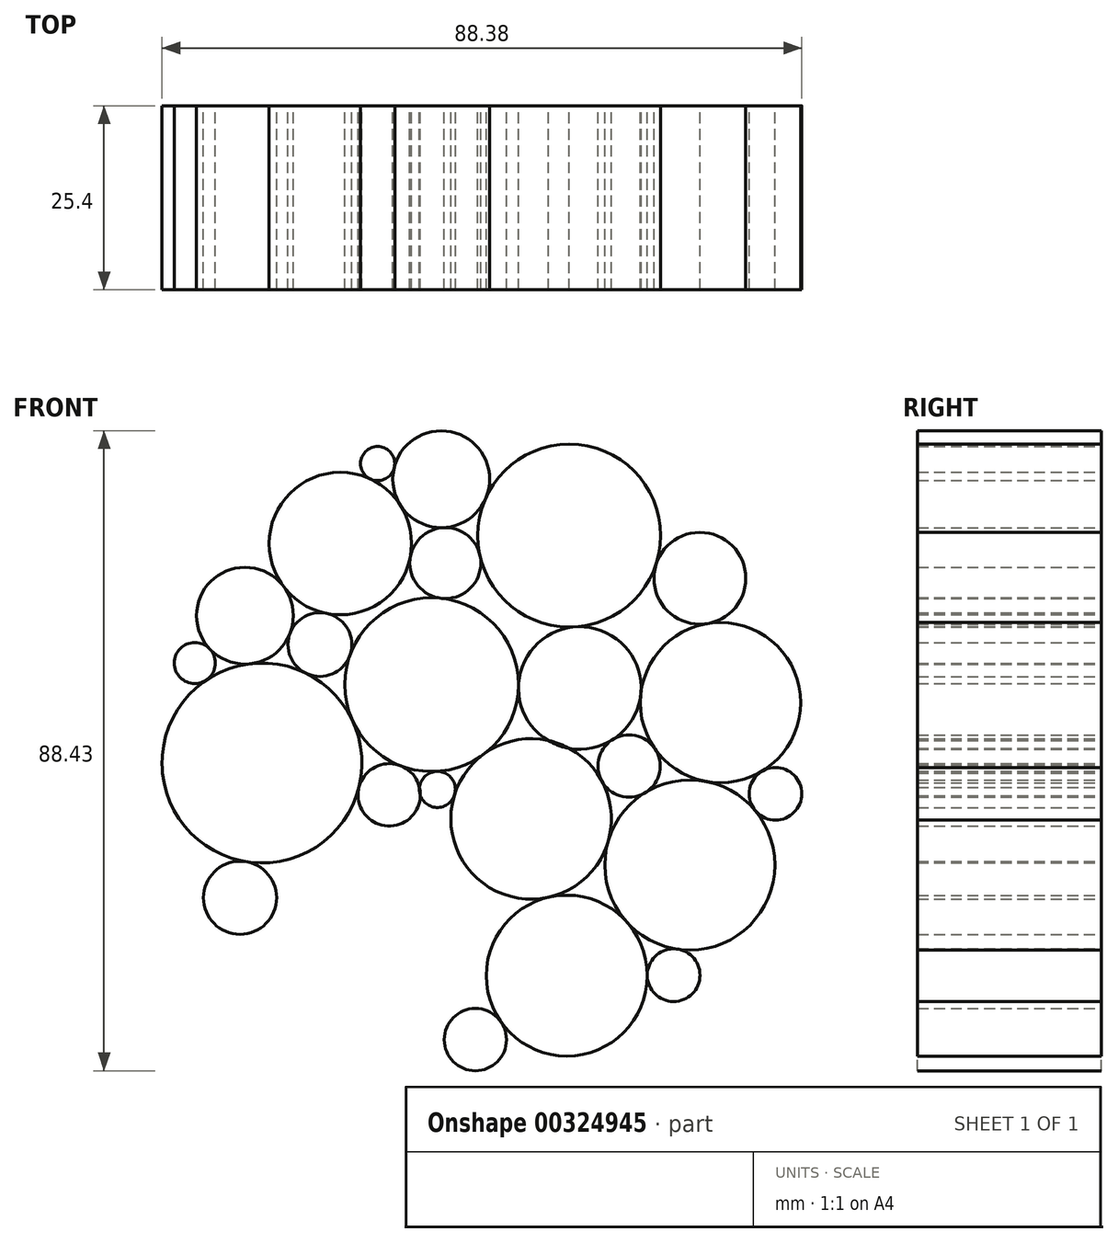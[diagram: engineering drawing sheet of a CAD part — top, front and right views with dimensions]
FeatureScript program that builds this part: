
annotation { "Feature Type Name" : "Feature", "Feature Type Description" : "" }
export const myFeature = defineFeature(function(context is Context, id is Id, definition is map)
    precondition{}
    {
        {
            var Q0;
            Q0=qCreatedBy(makeId("Front.planeOp"),FACE);
            var sketch = newSketch(context, id + "F0", { "sketchPlane" : qUnion([Q0])});
            skCircle(sketch, "E0", {"center": v(0, 0) * mm, "radius": 44.45 * mm});
            skCircle(sketch, "E1", {"center": v(-19.76, 28.42) * mm, "radius": 9.84 * mm});
            skPoint(sketch, "E1.first.point", {"position": v(-25.38, 36.5) * mm});
            skPoint(sketch, "E1.second.point", {"position": v(-25.38, 36.5) * mm});
            skPoint(sketch, "E1.third.point", {"position": v(-13.44, 20.87) * mm});
            skCircle(sketch, "E2", {"center": v(-32.95, 18.45) * mm, "radius": 6.69 * mm});
            skPoint(sketch, "E2.first.point", {"position": v(-27.61, 22.48) * mm});
            skPoint(sketch, "E2.second.point", {"position": v(-38.78, 21.72) * mm});
            skPoint(sketch, "E2.third.point", {"position": v(-30.05, 12.42) * mm});
            skCircle(sketch, "E3", {"center": v(-22.6, 14.46) * mm, "radius": 4.4 * mm});
            skPoint(sketch, "E3.first.point", {"position": v(-26.7, 16.05) * mm});
            skPoint(sketch, "E3.second.point", {"position": v(-21.72, 18.77) * mm});
            skPoint(sketch, "E3.third.point", {"position": v(-18.7, 12.42) * mm});
            skCircle(sketch, "E4", {"center": v(-5.83, 37.3) * mm, "radius": 6.7 * mm});
            skPoint(sketch, "E4.first.point", {"position": v(-6.86, 43.92) * mm});
            skPoint(sketch, "E4.second.point", {"position": v(-11.47, 33.7) * mm});
            skPoint(sketch, "E4.third.point", {"position": v(0, 34.02) * mm});
            skCircle(sketch, "E5", {"center": v(-5.26, 25.72) * mm, "radius": 4.9 * mm});
            skPoint(sketch, "E5.first.point", {"position": v(-5.5, 30.62) * mm});
            skPoint(sketch, "E5.second.point", {"position": v(-10.09, 26.62) * mm});
            skPoint(sketch, "E5.third.point", {"position": v(-0.38, 26.15) * mm});
            skCircle(sketch, "E6", {"center": v(-14.12, -25.7) * mm, "radius": 15.13 * mm});
            skPoint(sketch, "E6.first.point", {"position": v(-21.4, -38.96) * mm});
            skPoint(sketch, "E6.second.point", {"position": v(-21.4, -38.96) * mm});
            skPoint(sketch, "E6.third.point", {"position": v(-7.62, -12.04) * mm});
            skCircle(sketch, "E7", {"center": v(-30.59, -1.9) * mm, "radius": 13.8 * mm});
            skPoint(sketch, "E7.first.point", {"position": v(-44.33, -3.3) * mm});
            skPoint(sketch, "E7.second.point", {"position": v(-22.73, -13.26) * mm});
            skPoint(sketch, "E7.third.point", {"position": v(-32.18, 11.8) * mm});
            skCircle(sketch, "E8", {"center": v(-7.16, 8.92) * mm, "radius": 12 * mm});
            skPoint(sketch, "E8.first.point", {"position": v(-18.05, 3.89) * mm});
            skPoint(sketch, "E8.second.point", {"position": v(-18.45, 12.97) * mm});
            skPoint(sketch, "E8.third.point", {"position": v(-5.81, 20.85) * mm});
            skCircle(sketch, "E9", {"center": v(-13.01, -6.3) * mm, "radius": 4.3 * mm});
            skPoint(sketch, "E9.first.point", {"position": v(-11.47, -2.28) * mm});
            skPoint(sketch, "E9.second.point", {"position": v(-13.26, -10.6) * mm});
            skPoint(sketch, "E9.third.point", {"position": v(-17.2, -5.26) * mm});
            skCircle(sketch, "E10", {"center": v(-33.63, -20.53) * mm, "radius": 5.05 * mm});
            skPoint(sketch, "E10.first.point", {"position": v(-32.81, -15.54) * mm});
            skPoint(sketch, "E10.second.point", {"position": v(-28.74, -21.82) * mm});
            skPoint(sketch, "E10.third.point", {"position": v(-37.94, -23.16) * mm});
            skCircle(sketch, "E11", {"center": v(11.86, 29.52) * mm, "radius": 12.64 * mm});
            skPoint(sketch, "E11.first.point", {"position": v(16.57, 41.24) * mm});
            skPoint(sketch, "E11.second.point", {"position": v(0.3, 34.61) * mm});
            skPoint(sketch, "E11.third.point", {"position": v(17.65, 18.29) * mm});
            skCircle(sketch, "E12", {"center": v(6.59, -9.63) * mm, "radius": 11.09 * mm});
            skPoint(sketch, "E12.first.point", {"position": v(-0.01, -0.72) * mm});
            skPoint(sketch, "E12.second.point", {"position": v(-2.17, -16.43) * mm});
            skPoint(sketch, "E12.third.point", {"position": v(17.59, -8.25) * mm});
            skCircle(sketch, "E13", {"center": v(11.52, -31.28) * mm, "radius": 11.12 * mm});
            skPoint(sketch, "E13.first.point", {"position": v(0.66, -28.92) * mm});
            skPoint(sketch, "E13.second.point", {"position": v(9.05, -20.44) * mm});
            skPoint(sketch, "E13.third.point", {"position": v(15.36, -41.71) * mm});
            skCircle(sketch, "E14", {"center": v(13.31, 8.47) * mm, "radius": 8.47 * mm});
            skPoint(sketch, "E14.first.point", {"position": v(12.73, 16.91) * mm});
            skPoint(sketch, "E14.second.point", {"position": v(4.84, 8.65) * mm});
            skPoint(sketch, "E14.third.point", {"position": v(11.86, 0.12) * mm});
            skCircle(sketch, "E15", {"center": v(28.52, -16) * mm, "radius": 11.75 * mm});
            skPoint(sketch, "E15.first.point", {"position": v(17.24, -12.72) * mm});
            skPoint(sketch, "E15.second.point", {"position": v(19.78, -23.85) * mm});
            skPoint(sketch, "E15.third.point", {"position": v(38.77, -21.74) * mm});
            skCircle(sketch, "E16", {"center": v(32.75, 6.43) * mm, "radius": 11.07 * mm});
            skPoint(sketch, "E16.first.point", {"position": v(43.62, 8.57) * mm});
            skPoint(sketch, "E16.second.point", {"position": v(30.7, -4.45) * mm});
            skPoint(sketch, "E16.third.point", {"position": v(21.73, 7.58) * mm});
            skCircle(sketch, "E17", {"center": v(29.9, 23.62) * mm, "radius": 6.34 * mm});
            skPoint(sketch, "E17.first.point", {"position": v(23.87, 25.6) * mm});
            skPoint(sketch, "E17.second.point", {"position": v(30.94, 17.36) * mm});
            skPoint(sketch, "E17.third.point", {"position": v(34.88, 27.55) * mm});
            skCircle(sketch, "E18", {"center": v(-39.87, 11.91) * mm, "radius": 2.84 * mm});
            skPoint(sketch, "E18.first.point", {"position": v(-42.59, 12.72) * mm});
            skPoint(sketch, "E18.second.point", {"position": v(-37.8, 13.86) * mm});
            skPoint(sketch, "E18.third.point", {"position": v(-38.29, 9.56) * mm});
            skCircle(sketch, "E19", {"center": v(40.35, -6.16) * mm, "radius": 3.63 * mm});
            skPoint(sketch, "E19.first.point", {"position": v(38.47, -3.05) * mm});
            skPoint(sketch, "E19.second.point", {"position": v(37.56, -8.48) * mm});
            skPoint(sketch, "E19.third.point", {"position": v(43.94, -6.7) * mm});
            skCircle(sketch, "E20", {"center": v(-1.1, -40.13) * mm, "radius": 4.3 * mm});
            skPoint(sketch, "E20.first.point", {"position": v(2.42, -37.66) * mm});
            skPoint(sketch, "E20.second.point", {"position": v(-4, -36.93) * mm});
            skPoint(sketch, "E20.third.point", {"position": v(-1.23, -44.43) * mm});
            skCircle(sketch, "E21", {"center": v(20.12, -2.33) * mm, "radius": 4.3 * mm});
            skPoint(sketch, "E21.first.point", {"position": v(16.35, -4.37) * mm});
            skPoint(sketch, "E21.second.point", {"position": v(17.83, 1.3) * mm});
            skPoint(sketch, "E21.third.point", {"position": v(23.65, 0.12) * mm});
            skCircle(sketch, "E22", {"center": v(26.28, -31.22) * mm, "radius": 3.64 * mm});
            skPoint(sketch, "E22.first.point", {"position": v(26.8, -27.62) * mm});
            skPoint(sketch, "E22.second.point", {"position": v(22.63, -31.24) * mm});
            skPoint(sketch, "E22.third.point", {"position": v(28.62, -34) * mm});
            skCircle(sketch, "E23", {"center": v(-6.36, -5.55) * mm, "radius": 2.5 * mm});
            skPoint(sketch, "E23.first.point", {"position": v(-8.84, -5.26) * mm});
            skPoint(sketch, "E23.second.point", {"position": v(-6.5, -3.06) * mm});
            skPoint(sketch, "E23.third.point", {"position": v(-3.99, -6.3) * mm});
            skCircle(sketch, "E24", {"center": v(-14.61, 39.47) * mm, "radius": 2.36 * mm});
            skPoint(sketch, "E24.first.point", {"position": v(-15.43, 41.69) * mm});
            skPoint(sketch, "E24.second.point", {"position": v(-15.6, 37.34) * mm});
            skPoint(sketch, "E24.third.point", {"position": v(-12.32, 38.9) * mm});
            skPoint(sketch, "E25.third.point", {"position": v(-11.66, -40.62) * mm});
            skSolve(sketch);
        }
        {
            var Q0;
            {var subQ0=sQuery(id+"F0.wireOp",EDGE,"E1");var subQ4=makeQuery(id+"F0.imprint","INTERSECT",VERTEX,{"derivedFrom":[subQ0,sQuery(id+"F0.wireOp",EDGE,"E24")]});Q0=makeQuery(id+"F0.imprint","IMPRINT",FACE,{"disambiguationData":[TD([[makeQuery(id+"F0.imprint","IMPRINT",EDGE,{"disambiguationData":[TD([[subQ4,1.0]])],"derivedFrom":subQ0}),1.0]])]});}
            var Q1;
            {var subQ0=sQuery(id+"F0.wireOp",EDGE,"E24");var subQ1=makeQuery(id+"F0.imprint","INTERSECT",VERTEX,{"derivedFrom":[sQuery(id+"F0.wireOp",EDGE,"E0"),subQ0]});Q1=makeQuery(id+"F0.imprint","IMPRINT",FACE,{"disambiguationData":[TD([[makeQuery(id+"F0.imprint","IMPRINT",EDGE,{"disambiguationData":[TD([[subQ1,-1.0]])],"derivedFrom":subQ0}),1.0]])]});}
            var Q2;
            {var subQ0=sQuery(id+"F0.wireOp",EDGE,"E4");var subQ5=makeQuery(id+"F0.imprint","INTERSECT",VERTEX,{"derivedFrom":[sQuery(id+"F0.wireOp",EDGE,"E0"),subQ0]});Q2=makeQuery(id+"F0.imprint","IMPRINT",FACE,{"disambiguationData":[TD([[makeQuery(id+"F0.imprint","IMPRINT",EDGE,{"disambiguationData":[TD([[subQ5,-1.0]])],"derivedFrom":subQ0}),1.0]])]});}
            var Q3;
            {var subQ0=sQuery(id+"F0.wireOp",EDGE,"E5");var subQ1=makeQuery(id+"F0.imprint","INTERSECT",VERTEX,{"derivedFrom":[sQuery(id+"F0.wireOp",EDGE,"E4"),subQ0]});Q3=makeQuery(id+"F0.imprint","IMPRINT",FACE,{"disambiguationData":[TD([[makeQuery(id+"F0.imprint","IMPRINT",EDGE,{"disambiguationData":[TD([[subQ1,1.0]])],"derivedFrom":subQ0}),1.0]])]});}
            var Q4;
            {var subQ0=sQuery(id+"F0.wireOp",EDGE,"E11");var subQ5=makeQuery(id+"F0.imprint","INTERSECT",VERTEX,{"derivedFrom":[sQuery(id+"F0.wireOp",EDGE,"E0"),subQ0]});Q4=makeQuery(id+"F0.imprint","IMPRINT",FACE,{"disambiguationData":[TD([[makeQuery(id+"F0.imprint","IMPRINT",EDGE,{"disambiguationData":[TD([[subQ5,-1.0]])],"derivedFrom":subQ0}),1.0]])]});}
            var Q5;
            {var subQ0=sQuery(id+"F0.wireOp",EDGE,"E8");var subQ4=makeQuery(id+"F0.imprint","INTERSECT",VERTEX,{"derivedFrom":[sQuery(id+"F0.wireOp",EDGE,"E3"),subQ0]});Q5=makeQuery(id+"F0.imprint","IMPRINT",FACE,{"disambiguationData":[TD([[makeQuery(id+"F0.imprint","IMPRINT",EDGE,{"disambiguationData":[TD([[subQ4,1.0]])],"derivedFrom":subQ0}),1.0]])]});}
            var Q6;
            {var subQ0=sQuery(id+"F0.wireOp",EDGE,"E6");var subQ4=makeQuery(id+"F0.imprint","INTERSECT",VERTEX,{"derivedFrom":[sQuery(id+"F0.wireOp",EDGE,"E9"),subQ0]});Q6=makeQuery(id+"F0.imprint","IMPRINT",FACE,{"disambiguationData":[TD([[makeQuery(id+"F0.imprint","IMPRINT",EDGE,{"disambiguationData":[TD([[subQ4,1.0]])],"derivedFrom":subQ0}),1.0]])]});}
            var Q7;
            {var subQ0=sQuery(id+"F0.wireOp",EDGE,"E12");var subQ4=sQuery(id+"F0.wireOp",EDGE,"E14");var subQ6=makeQuery(id+"F0.imprint","INTERSECT",VERTEX,{"disambiguationData":[OD(0.0)],"derivedFrom":[subQ0,subQ4]});Q7=makeQuery(id+"F0.imprint","IMPRINT",FACE,{"disambiguationData":[TD([[makeQuery(id+"F0.imprint","IMPRINT",EDGE,{"disambiguationData":[TD([[subQ6,1.0]])],"derivedFrom":subQ0}),1.0]])]});}
            var Q8;
            {var subQ0=sQuery(id+"F0.wireOp",EDGE,"E14");var subQ1=sQuery(id+"F0.wireOp",EDGE,"E12");var subQ2=makeQuery(id+"F0.imprint","INTERSECT",VERTEX,{"disambiguationData":[OD(0.0)],"derivedFrom":[subQ1,subQ0]});Q8=makeQuery(id+"F0.imprint","IMPRINT",FACE,{"disambiguationData":[TD([[makeQuery(id+"F0.imprint","IMPRINT",EDGE,{"disambiguationData":[TD([[subQ2,-1.0]])],"derivedFrom":subQ1}),-1.0]])]});}
            var Q9;
            {var subQ0=sQuery(id+"F0.wireOp",EDGE,"E9");var subQ5=makeQuery(id+"F0.imprint","INTERSECT",VERTEX,{"derivedFrom":[sQuery(id+"F0.wireOp",EDGE,"E8"),subQ0]});Q9=makeQuery(id+"F0.imprint","IMPRINT",FACE,{"disambiguationData":[TD([[makeQuery(id+"F0.imprint","IMPRINT",EDGE,{"disambiguationData":[TD([[subQ5,1.0]])],"derivedFrom":subQ0}),1.0]])]});}
            var Q10;
            {var subQ0=sQuery(id+"F0.wireOp",EDGE,"E23");var subQ1=sQuery(id+"F0.wireOp",EDGE,"E9");var subQ2=makeQuery(id+"F0.imprint","INTERSECT",VERTEX,{"disambiguationData":[OD(0.0)],"derivedFrom":[subQ1,subQ0]});Q10=makeQuery(id+"F0.imprint","IMPRINT",FACE,{"disambiguationData":[TD([[makeQuery(id+"F0.imprint","IMPRINT",EDGE,{"disambiguationData":[TD([[subQ2,1.0]])],"derivedFrom":subQ1}),-1.0]])]});}
            var Q11;
            {var subQ0=sQuery(id+"F0.wireOp",EDGE,"E7");var subQ4=sQuery(id+"F0.wireOp",EDGE,"E0");var subQ5=makeQuery(id+"F0.imprint","INTERSECT",VERTEX,{"disambiguationData":[OD(0.0)],"derivedFrom":[subQ4,subQ0]});Q11=makeQuery(id+"F0.imprint","IMPRINT",FACE,{"disambiguationData":[TD([[makeQuery(id+"F0.imprint","IMPRINT",EDGE,{"disambiguationData":[TD([[subQ5,-1.0]])],"derivedFrom":subQ4}),1.0]])]});}
            var Q12;
            {var subQ0=sQuery(id+"F0.wireOp",EDGE,"E10");var subQ1=makeQuery(id+"F0.imprint","INTERSECT",VERTEX,{"derivedFrom":[sQuery(id+"F0.wireOp",EDGE,"E0"),subQ0]});Q12=makeQuery(id+"F0.imprint","IMPRINT",FACE,{"disambiguationData":[TD([[makeQuery(id+"F0.imprint","IMPRINT",EDGE,{"disambiguationData":[TD([[subQ1,1.0]])],"derivedFrom":subQ0}),1.0]])]});}
            var Q13;
            {var subQ0=sQuery(id+"F0.wireOp",EDGE,"E3");var subQ1=makeQuery(id+"F0.imprint","INTERSECT",VERTEX,{"derivedFrom":[sQuery(id+"F0.wireOp",EDGE,"E1"),subQ0]});Q13=makeQuery(id+"F0.imprint","IMPRINT",FACE,{"disambiguationData":[TD([[makeQuery(id+"F0.imprint","IMPRINT",EDGE,{"disambiguationData":[TD([[subQ1,-1.0]])],"derivedFrom":subQ0}),1.0]])]});}
            var Q14;
            {var subQ0=sQuery(id+"F0.wireOp",EDGE,"E2");var subQ4=makeQuery(id+"F0.imprint","INTERSECT",VERTEX,{"derivedFrom":[sQuery(id+"F0.wireOp",EDGE,"E0"),subQ0]});Q14=makeQuery(id+"F0.imprint","IMPRINT",FACE,{"disambiguationData":[TD([[makeQuery(id+"F0.imprint","IMPRINT",EDGE,{"disambiguationData":[TD([[subQ4,1.0]])],"derivedFrom":subQ0}),1.0]])]});}
            var Q15;
            {var subQ0=sQuery(id+"F0.wireOp",EDGE,"E18");var subQ1=makeQuery(id+"F0.imprint","INTERSECT",VERTEX,{"derivedFrom":[sQuery(id+"F0.wireOp",EDGE,"E0"),subQ0]});Q15=makeQuery(id+"F0.imprint","IMPRINT",FACE,{"disambiguationData":[TD([[makeQuery(id+"F0.imprint","IMPRINT",EDGE,{"disambiguationData":[TD([[subQ1,1.0]])],"derivedFrom":subQ0}),1.0]])]});}
            var Q16;
            {var subQ0=sQuery(id+"F0.wireOp",EDGE,"E16");var subQ5=makeQuery(id+"F0.imprint","INTERSECT",VERTEX,{"derivedFrom":[sQuery(id+"F0.wireOp",EDGE,"E0"),subQ0]});Q16=makeQuery(id+"F0.imprint","IMPRINT",FACE,{"disambiguationData":[TD([[makeQuery(id+"F0.imprint","IMPRINT",EDGE,{"disambiguationData":[TD([[subQ5,-1.0]])],"derivedFrom":subQ0}),1.0]])]});}
            var Q17;
            {var subQ0=sQuery(id+"F0.wireOp",EDGE,"E17");var subQ1=makeQuery(id+"F0.imprint","INTERSECT",VERTEX,{"derivedFrom":[sQuery(id+"F0.wireOp",EDGE,"E0"),subQ0]});Q17=makeQuery(id+"F0.imprint","IMPRINT",FACE,{"disambiguationData":[TD([[makeQuery(id+"F0.imprint","IMPRINT",EDGE,{"disambiguationData":[TD([[subQ1,-1.0]])],"derivedFrom":subQ0}),1.0]])]});}
            var Q18;
            {var subQ0=sQuery(id+"F0.wireOp",EDGE,"E21");var subQ1=makeQuery(id+"F0.imprint","INTERSECT",VERTEX,{"derivedFrom":[sQuery(id+"F0.wireOp",EDGE,"E14"),subQ0]});Q18=makeQuery(id+"F0.imprint","IMPRINT",FACE,{"disambiguationData":[TD([[makeQuery(id+"F0.imprint","IMPRINT",EDGE,{"disambiguationData":[TD([[subQ1,1.0]])],"derivedFrom":subQ0}),1.0]])]});}
            var Q19;
            {var subQ0=sQuery(id+"F0.wireOp",EDGE,"E15");var subQ4=makeQuery(id+"F0.imprint","INTERSECT",VERTEX,{"derivedFrom":[subQ0,sQuery(id+"F0.wireOp",EDGE,"E16")]});Q19=makeQuery(id+"F0.imprint","IMPRINT",FACE,{"disambiguationData":[TD([[makeQuery(id+"F0.imprint","IMPRINT",EDGE,{"disambiguationData":[TD([[subQ4,1.0]])],"derivedFrom":subQ0}),1.0]])]});}
            var Q20;
            {var subQ0=sQuery(id+"F0.wireOp",EDGE,"E13");var subQ4=makeQuery(id+"F0.imprint","INTERSECT",VERTEX,{"derivedFrom":[subQ0,sQuery(id+"F0.wireOp",EDGE,"E15")]});Q20=makeQuery(id+"F0.imprint","IMPRINT",FACE,{"disambiguationData":[TD([[makeQuery(id+"F0.imprint","IMPRINT",EDGE,{"disambiguationData":[TD([[subQ4,1.0]])],"derivedFrom":subQ0}),1.0]])]});}
            var Q21;
            {var subQ0=sQuery(id+"F0.wireOp",EDGE,"E20");var subQ1=makeQuery(id+"F0.imprint","INTERSECT",VERTEX,{"derivedFrom":[sQuery(id+"F0.wireOp",EDGE,"E13"),subQ0]});Q21=makeQuery(id+"F0.imprint","IMPRINT",FACE,{"disambiguationData":[TD([[makeQuery(id+"F0.imprint","IMPRINT",EDGE,{"disambiguationData":[TD([[subQ1,-1.0]])],"derivedFrom":subQ0}),1.0]])]});}
            var Q22;
            {var subQ0=sQuery(id+"F0.wireOp",EDGE,"E22");var subQ1=makeQuery(id+"F0.imprint","INTERSECT",VERTEX,{"derivedFrom":[sQuery(id+"F0.wireOp",EDGE,"E13"),subQ0]});Q22=makeQuery(id+"F0.imprint","IMPRINT",FACE,{"disambiguationData":[TD([[makeQuery(id+"F0.imprint","IMPRINT",EDGE,{"disambiguationData":[TD([[subQ1,1.0]])],"derivedFrom":subQ0}),1.0]])]});}
            var Q23;
            {var subQ0=sQuery(id+"F0.wireOp",EDGE,"E19");var subQ1=makeQuery(id+"F0.imprint","INTERSECT",VERTEX,{"derivedFrom":[sQuery(id+"F0.wireOp",EDGE,"E15"),subQ0]});Q23=makeQuery(id+"F0.imprint","IMPRINT",FACE,{"disambiguationData":[TD([[makeQuery(id+"F0.imprint","IMPRINT",EDGE,{"disambiguationData":[TD([[subQ1,1.0]])],"derivedFrom":subQ0}),1.0]])]});}
            extrude(context, id + "F1", {"entities" : qUnion([Q0, Q1, Q2, Q3, Q4, Q5, Q6, Q7, Q8, Q9, Q10, Q11, Q12, Q13, Q14, Q15, Q16, Q17, Q18, Q19, Q20, Q21, Q22, Q23]), "depth" : 25.4 * mm});
        }
    });
